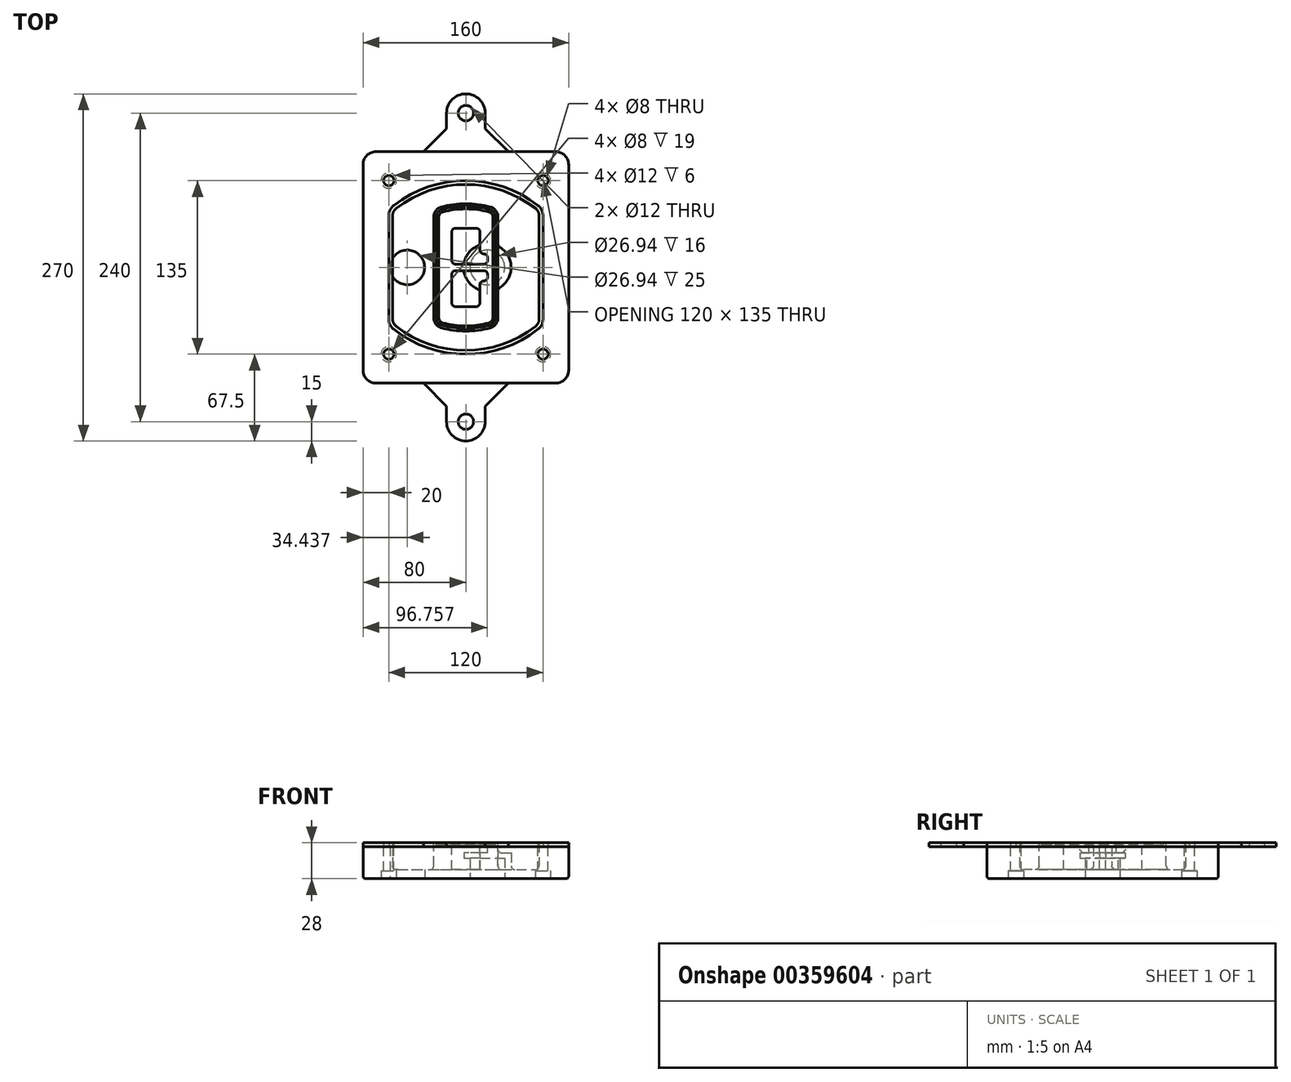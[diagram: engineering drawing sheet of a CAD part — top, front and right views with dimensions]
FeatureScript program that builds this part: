
annotation { "Feature Type Name" : "Feature", "Feature Type Description" : "" }
export const myFeature = defineFeature(function(context is Context, id is Id, definition is map)
    precondition{}
    {
        {
            var Q0;
            Q0=qCreatedBy(makeId("Top.planeOp"),FACE);
            var sketch = newSketch(context, id + "F0", { "sketchPlane" : qUnion([Q0])});
            skPoint(sketch, "E0.rect.middle", {"position": v(0, 0) * mm});
            skLineSegment(sketch, "E1.bottom", {"start": v(-70, -90) * mm, "end": v(70, -90) * mm});
            skLineSegment(sketch, "E1.top", {"start": v(-70, 90) * mm, "end": v(70, 90) * mm});
            skLineSegment(sketch, "E1.left", {"start": v(-80, -80) * mm, "end": v(-80, 80) * mm});
            skLineSegment(sketch, "E1.right", {"start": v(80, -80) * mm, "end": v(80, 80) * mm});
            skLineSegment(sketch, "E2", {"start": v(-80, 90) * mm, "end": v(80, -90) * mm, "construction": true});
            skLineSegment(sketch, "E3", {"start": v(80, 90) * mm, "end": v(-80, -90) * mm, "construction": true});
            skCircle(sketch, "E4", {"center": v(-60, 67.5) * mm, "radius": 4 * mm});
            skCircle(sketch, "E5", {"center": v(60, 67.5) * mm, "radius": 4 * mm});
            skCircle(sketch, "E6", {"center": v(60, -67.5) * mm, "radius": 4 * mm});
            skCircle(sketch, "E7", {"center": v(-60, -67.5) * mm, "radius": 4 * mm});
            skLineSegment(sketch, "E8", {"start": v(-60, 67.5) * mm, "end": v(60, 67.5) * mm, "construction": true});
            skLineSegment(sketch, "E9", {"start": v(60, 67.5) * mm, "end": v(60, -67.5) * mm, "construction": true});
            skLineSegment(sketch, "E10", {"start": v(60, -67.5) * mm, "end": v(-60, -67.5) * mm, "construction": true});
            skLineSegment(sketch, "E11", {"start": v(-60, -67.5) * mm, "end": v(-60, 67.5) * mm, "construction": true});
            skLineSegment(sketch, "E12", {"start": v(-60, 40.3) * mm, "end": v(-60, -40.3) * mm});
            skLineSegment(sketch, "E13", {"start": v(60, 40.3) * mm, "end": v(60, -40.3) * mm});
            skArc(sketch, "E14", {"start": v(56.15, 48.18) * mm, "mid": v(0, 67.5) * mm, "end": v(-56.15, 48.18) * mm});
            skArc(sketch, "E15", {"start": v(-56.15, -48.18) * mm, "mid": v(0, -67.5) * mm, "end": v(56.15, -48.18) * mm});
            skLineSegment(sketch, "E16", {"start": v(-60, 0) * mm, "end": v(60, 0) * mm, "construction": true});
            skPoint(sketch, "E17.visualSharp", {"position": v(-60, -45) * mm});
            skArc(sketch, "E17.filletArc", {"start": v(-60, -40.3) * mm, "mid": v(-58.99, -44.68) * mm, "end": v(-56.15, -48.18) * mm});
            skPoint(sketch, "E18.visualSharp", {"position": v(-60, 45) * mm});
            skArc(sketch, "E18.filletArc", {"start": v(-56.15, 48.18) * mm, "mid": v(-58.99, 44.68) * mm, "end": v(-60, 40.3) * mm});
            skPoint(sketch, "E19.visualSharp", {"position": v(60, 45) * mm});
            skArc(sketch, "E19.filletArc", {"start": v(60, 40.3) * mm, "mid": v(58.99, 44.68) * mm, "end": v(56.15, 48.18) * mm});
            skPoint(sketch, "E20.visualSharp", {"position": v(60, -45) * mm});
            skArc(sketch, "E20.filletArc", {"start": v(56.15, -48.18) * mm, "mid": v(58.99, -44.68) * mm, "end": v(60, -40.3) * mm});
            skPoint(sketch, "E21.visualSharp", {"position": v(-80, 90) * mm});
            skArc(sketch, "E21.filletArc", {"start": v(-70, 90) * mm, "mid": v(-77.07, 87.07) * mm, "end": v(-80, 80) * mm});
            skPoint(sketch, "E22.visualSharp", {"position": v(80, 90) * mm});
            skArc(sketch, "E22.filletArc", {"start": v(80, 80) * mm, "mid": v(77.07, 87.07) * mm, "end": v(70, 90) * mm});
            skPoint(sketch, "E23.visualSharp", {"position": v(80, -90) * mm});
            skArc(sketch, "E23.filletArc", {"start": v(70, -90) * mm, "mid": v(77.07, -87.07) * mm, "end": v(80, -80) * mm});
            skPoint(sketch, "E24.visualSharp", {"position": v(-80, -90) * mm});
            skArc(sketch, "E24.filletArc", {"start": v(-80, -80) * mm, "mid": v(-77.07, -87.07) * mm, "end": v(-70, -90) * mm});
            skArc(sketch, "E25.0", {"start": v(57, 40.3) * mm, "mid": v(56.3, 43.36) * mm, "end": v(54.3, 45.81) * mm});
            skLineSegment(sketch, "E25.1", {"start": v(57, 40.3) * mm, "end": v(57, -40.3) * mm});
            skArc(sketch, "E25.2", {"start": v(54.3, -45.81) * mm, "mid": v(56.3, -43.36) * mm, "end": v(57, -40.3) * mm});
            skArc(sketch, "E25.3", {"start": v(-54.3, -45.81) * mm, "mid": v(0, -64.5) * mm, "end": v(54.3, -45.81) * mm});
            skArc(sketch, "E25.4", {"start": v(-57, -40.3) * mm, "mid": v(-56.3, -43.36) * mm, "end": v(-54.3, -45.81) * mm});
            skArc(sketch, "E25.5", {"start": v(54.3, 45.81) * mm, "mid": v(0, 64.5) * mm, "end": v(-54.3, 45.81) * mm});
            skLineSegment(sketch, "E25.6", {"start": v(-57, 40.3) * mm, "end": v(-57, -40.3) * mm});
            skArc(sketch, "E25.7", {"start": v(-54.3, 45.81) * mm, "mid": v(-56.3, 43.36) * mm, "end": v(-57, 40.3) * mm});
            skArc(sketch, "E26.0", {"start": v(-58.62, 51.33) * mm, "mid": v(-62.58, 46.43) * mm, "end": v(-64, 40.3) * mm});
            skArc(sketch, "E26.1", {"start": v(58.62, 51.33) * mm, "mid": v(0, 71.5) * mm, "end": v(-58.62, 51.33) * mm});
            skArc(sketch, "E26.2", {"start": v(64, 40.3) * mm, "mid": v(62.58, 46.43) * mm, "end": v(58.62, 51.33) * mm});
            skLineSegment(sketch, "E26.3", {"start": v(64, 40.3) * mm, "end": v(64, -40.3) * mm});
            skArc(sketch, "E26.4", {"start": v(58.62, -51.33) * mm, "mid": v(62.58, -46.43) * mm, "end": v(64, -40.3) * mm});
            skLineSegment(sketch, "E26.5", {"start": v(-64, 40.3) * mm, "end": v(-64, -40.3) * mm});
            skArc(sketch, "E26.6", {"start": v(-58.62, -51.33) * mm, "mid": v(0, -71.5) * mm, "end": v(58.62, -51.33) * mm});
            skArc(sketch, "E26.7", {"start": v(-64, -40.3) * mm, "mid": v(-62.58, -46.43) * mm, "end": v(-58.62, -51.33) * mm});
            skSolve(sketch);
        }
        {
            var Q0;
            Q0=makeQuery(id+"F0.imprint","IMPRINT",FACE,{"disambiguationData":[TD([[makeQuery(id+"F0.imprint","IMPRINT",EDGE,{"derivedFrom":sQuery(id+"F0.wireOp",EDGE,"E1.bottom")}),1.0]])]});
            var Q1;
            Q1=makeQuery(id+"F0.imprint","IMPRINT",FACE,{"disambiguationData":[TD([[makeQuery(id+"F0.imprint","IMPRINT",EDGE,{"derivedFrom":sQuery(id+"F0.wireOp",EDGE,"E12")}),1.0]])]});
            var Q2;
            Q2=makeQuery(id+"F0.imprint","IMPRINT",FACE,{"disambiguationData":[TD([[makeQuery(id+"F0.imprint","IMPRINT",EDGE,{"derivedFrom":sQuery(id+"F0.wireOp",EDGE,"E25.0")}),1.0]])]});
            var Q3;
            Q3=makeQuery(id+"F0.imprint","IMPRINT",FACE,{"disambiguationData":[TD([[makeQuery(id+"F0.imprint","IMPRINT",EDGE,{"derivedFrom":sQuery(id+"F0.wireOp",EDGE,"E12")}),-1.0]])]});
            extrude(context, id + "F1", {"entities" : qUnion([Q0, Q1, Q2, Q3]), "oppositeDirection" : true, "depth" : 25 * mm});
        }
        {
            var Q0;
            Q0=makeQuery(id+"F0.imprint","IMPRINT",FACE,{"disambiguationData":[TD([[makeQuery(id+"F0.imprint","IMPRINT",EDGE,{"derivedFrom":sQuery(id+"F0.wireOp",EDGE,"E12")}),1.0]])]});
            extrude(context, id + "F2", {"entities" : qUnion([Q0]), "operationType" : NewBodyOperationType.ADD, "depth" : 3 * mm});
        }
        {
            var Q0;
            Q0=makeQuery(id+"F0.imprint","IMPRINT",FACE,{"disambiguationData":[TD([[makeQuery(id+"F0.imprint","IMPRINT",EDGE,{"derivedFrom":sQuery(id+"F0.wireOp",EDGE,"E25.0")}),1.0]])]});
            extrude(context, id + "F3", {"entities" : qUnion([Q0]), "operationType" : NewBodyOperationType.REMOVE, "oppositeDirection" : true, "depth" : 18 * mm});
        }
        {
            var Q0;
            Q0=makeQuery(id+"F2.opExtrude","CAP_FACE",FACE,{"disambiguationData":[OSD([sQuery(id+"F0.wireOp",EDGE,"E12"),sQuery(id+"F0.wireOp",EDGE,"E13"),sQuery(id+"F0.wireOp",EDGE,"E14"),sQuery(id+"F0.wireOp",EDGE,"E15"),sQuery(id+"F0.wireOp",EDGE,"E17.filletArc"),sQuery(id+"F0.wireOp",EDGE,"E18.filletArc"),sQuery(id+"F0.wireOp",EDGE,"E19.filletArc"),sQuery(id+"F0.wireOp",EDGE,"E20.filletArc"),sQuery(id+"F0.wireOp",EDGE,"E25.0"),sQuery(id+"F0.wireOp",EDGE,"E25.1"),sQuery(id+"F0.wireOp",EDGE,"E25.2"),sQuery(id+"F0.wireOp",EDGE,"E25.3"),sQuery(id+"F0.wireOp",EDGE,"E25.4"),sQuery(id+"F0.wireOp",EDGE,"E25.5"),sQuery(id+"F0.wireOp",EDGE,"E25.6"),sQuery(id+"F0.wireOp",EDGE,"E25.7")])],"isStart":false});
            var sketch = newSketch(context, id + "F4", { "sketchPlane" : qUnion([Q0])});
            skArc(sketch, "E27.0", {"start": v(-19.08, -46.97) * mm, "mid": v(0, -49.5) * mm, "end": v(19.08, -46.97) * mm});
            skArc(sketch, "E28.0", {"start": v(19.08, 46.97) * mm, "mid": v(0, 49.5) * mm, "end": v(-19.08, 46.97) * mm});
            skLineSegment(sketch, "E29", {"start": v(-25, 39.25) * mm, "end": v(-25, -39.25) * mm});
            skLineSegment(sketch, "E30", {"start": v(25, 39.25) * mm, "end": v(25, -39.25) * mm});
            skLineSegment(sketch, "E31", {"start": v(-25, 45.1) * mm, "end": v(25, 45.1) * mm, "construction": true});
            skLineSegment(sketch, "E32", {"start": v(-25, -45.1) * mm, "end": v(25, -45.1) * mm, "construction": true});
            skPoint(sketch, "E33.visualSharp", {"position": v(-25, 45.1) * mm});
            skArc(sketch, "E33.filletArc", {"start": v(-19.08, 46.97) * mm, "mid": v(-23.35, 44.11) * mm, "end": v(-25, 39.25) * mm});
            skPoint(sketch, "E34.visualSharp", {"position": v(25, 45.1) * mm});
            skArc(sketch, "E34.filletArc", {"start": v(25, 39.25) * mm, "mid": v(23.35, 44.11) * mm, "end": v(19.08, 46.97) * mm});
            skPoint(sketch, "E35.visualSharp", {"position": v(25, -45.1) * mm});
            skArc(sketch, "E35.filletArc", {"start": v(19.08, -46.97) * mm, "mid": v(23.35, -44.11) * mm, "end": v(25, -39.25) * mm});
            skPoint(sketch, "E36.visualSharp", {"position": v(-25, -45.1) * mm});
            skArc(sketch, "E36.filletArc", {"start": v(-25, -39.25) * mm, "mid": v(-23.35, -44.11) * mm, "end": v(-19.08, -46.97) * mm});
            skArc(sketch, "E37.0", {"start": v(54.3, 45.81) * mm, "mid": v(0, 64.5) * mm, "end": v(-54.3, 45.81) * mm});
            skArc(sketch, "E37.1", {"start": v(-54.3, 45.81) * mm, "mid": v(-56.3, 43.36) * mm, "end": v(-57, 40.3) * mm});
            skLineSegment(sketch, "E37.2", {"start": v(-57, 40.3) * mm, "end": v(-57, -40.3) * mm});
            skArc(sketch, "E37.3", {"start": v(-57, -40.3) * mm, "mid": v(-56.3, -43.36) * mm, "end": v(-54.3, -45.81) * mm});
            skArc(sketch, "E37.4", {"start": v(-54.3, -45.81) * mm, "mid": v(0, -64.5) * mm, "end": v(54.3, -45.81) * mm});
            skArc(sketch, "E37.5", {"start": v(54.3, -45.81) * mm, "mid": v(56.3, -43.36) * mm, "end": v(57, -40.3) * mm});
            skLineSegment(sketch, "E37.6", {"start": v(57, 40.3) * mm, "end": v(57, -40.3) * mm});
            skArc(sketch, "E37.7", {"start": v(57, 40.3) * mm, "mid": v(56.3, 43.36) * mm, "end": v(54.3, 45.81) * mm});
            skLineSegment(sketch, "E38.0", {"start": v(23, 39.25) * mm, "end": v(23, -39.25) * mm});
            skArc(sketch, "E38.1", {"start": v(18.56, -45.04) * mm, "mid": v(21.76, -42.9) * mm, "end": v(23, -39.25) * mm});
            skArc(sketch, "E38.2", {"start": v(-18.56, -45.04) * mm, "mid": v(0, -47.5) * mm, "end": v(18.56, -45.04) * mm});
            skArc(sketch, "E38.3", {"start": v(-23, -39.25) * mm, "mid": v(-21.76, -42.9) * mm, "end": v(-18.56, -45.04) * mm});
            skLineSegment(sketch, "E38.4", {"start": v(-23, 39.25) * mm, "end": v(-23, -39.25) * mm});
            skArc(sketch, "E38.5", {"start": v(23, 39.25) * mm, "mid": v(21.76, 42.9) * mm, "end": v(18.56, 45.04) * mm});
            skArc(sketch, "E38.6", {"start": v(-18.56, 45.04) * mm, "mid": v(-21.76, 42.9) * mm, "end": v(-23, 39.25) * mm});
            skArc(sketch, "E38.7", {"start": v(18.56, 45.04) * mm, "mid": v(0, 47.5) * mm, "end": v(-18.56, 45.04) * mm});
            skArc(sketch, "E39.0", {"start": v(21, 39.25) * mm, "mid": v(20.18, 41.68) * mm, "end": v(18.04, 43.1) * mm});
            skLineSegment(sketch, "E39.1", {"start": v(21, 39.25) * mm, "end": v(21, -39.25) * mm});
            skArc(sketch, "E39.2", {"start": v(18.04, -43.1) * mm, "mid": v(20.18, -41.68) * mm, "end": v(21, -39.25) * mm});
            skArc(sketch, "E39.3", {"start": v(-18.04, -43.1) * mm, "mid": v(0, -45.5) * mm, "end": v(18.04, -43.1) * mm});
            skArc(sketch, "E39.4", {"start": v(-21, -39.25) * mm, "mid": v(-20.18, -41.68) * mm, "end": v(-18.04, -43.1) * mm});
            skArc(sketch, "E39.5", {"start": v(18.04, 43.1) * mm, "mid": v(0, 45.5) * mm, "end": v(-18.04, 43.1) * mm});
            skLineSegment(sketch, "E39.6", {"start": v(-21, 39.25) * mm, "end": v(-21, -39.25) * mm});
            skArc(sketch, "E39.7", {"start": v(-18.04, 43.1) * mm, "mid": v(-20.18, 41.68) * mm, "end": v(-21, 39.25) * mm});
            skLineSegment(sketch, "E40", {"start": v(-25, 0) * mm, "end": v(25, 0) * mm, "construction": true});
            skLineSegment(sketch, "E41", {"start": v(-11, 5.5) * mm, "end": v(-11, 27.5) * mm});
            skLineSegment(sketch, "E42", {"start": v(-8, 30.5) * mm, "end": v(8, 30.5) * mm});
            skLineSegment(sketch, "E43", {"start": v(11, 27.5) * mm, "end": v(11, 13.5) * mm});
            skLineSegment(sketch, "E44", {"start": v(14, 10.5) * mm, "end": v(14, 10.5) * mm});
            skLineSegment(sketch, "E45", {"start": v(17, 7.5) * mm, "end": v(17, 5.5) * mm});
            skLineSegment(sketch, "E46", {"start": v(14, 2.5) * mm, "end": v(-8, 2.5) * mm});
            skPoint(sketch, "E47.visualSharp", {"position": v(-11, 30.5) * mm});
            skArc(sketch, "E47.filletArc", {"start": v(-8, 30.5) * mm, "mid": v(-10.12, 29.62) * mm, "end": v(-11, 27.5) * mm});
            skPoint(sketch, "E48.visualSharp", {"position": v(11, 30.5) * mm});
            skArc(sketch, "E48.filletArc", {"start": v(11, 27.5) * mm, "mid": v(10.12, 29.62) * mm, "end": v(8, 30.5) * mm});
            skPoint(sketch, "E49.visualSharp", {"position": v(11, 10.5) * mm});
            skArc(sketch, "E49.filletArc", {"start": v(11, 13.5) * mm, "mid": v(11.88, 11.38) * mm, "end": v(14, 10.5) * mm});
            skPoint(sketch, "E50.visualSharp", {"position": v(17, 10.5) * mm});
            skArc(sketch, "E50.filletArc", {"start": v(17, 7.5) * mm, "mid": v(16.12, 9.62) * mm, "end": v(14, 10.5) * mm});
            skPoint(sketch, "E51.visualSharp", {"position": v(17, 2.5) * mm});
            skArc(sketch, "E51.filletArc", {"start": v(14, 2.5) * mm, "mid": v(16.12, 3.38) * mm, "end": v(17, 5.5) * mm});
            skPoint(sketch, "E52.visualSharp", {"position": v(-11, 2.5) * mm});
            skArc(sketch, "E52.filletArc", {"start": v(-11, 5.5) * mm, "mid": v(-10.12, 3.38) * mm, "end": v(-8, 2.5) * mm});
            skLineSegment(sketch, "E53.0.MirrorCS", {"start": v(14, -2.5) * mm, "end": v(-8, -2.5) * mm});
            skArc(sketch, "E54.0.MirrorCS", {"start": v(-11, -5.5) * mm, "mid": v(-10.12, -3.38) * mm, "end": v(-8, -2.5) * mm});
            skLineSegment(sketch, "E55.0.MirrorCS", {"start": v(-11, -5.5) * mm, "end": v(-11, -27.5) * mm});
            skArc(sketch, "E56.0.MirrorCS", {"start": v(-8, -30.5) * mm, "mid": v(-10.12, -29.62) * mm, "end": v(-11, -27.5) * mm});
            skLineSegment(sketch, "E57.0.MirrorCS", {"start": v(-8, -30.5) * mm, "end": v(8, -30.5) * mm});
            skArc(sketch, "E58.0.MirrorCS", {"start": v(11, -27.5) * mm, "mid": v(10.12, -29.62) * mm, "end": v(8, -30.5) * mm});
            skLineSegment(sketch, "E59.0.MirrorCS", {"start": v(11, -27.5) * mm, "end": v(11, -13.5) * mm});
            skArc(sketch, "E60.0.MirrorCS", {"start": v(11, -13.5) * mm, "mid": v(11.88, -11.38) * mm, "end": v(14, -10.5) * mm});
            skArc(sketch, "E61.0.MirrorCS", {"start": v(17, -7.5) * mm, "mid": v(16.12, -9.62) * mm, "end": v(14, -10.5) * mm});
            skLineSegment(sketch, "E62.0.MirrorCS", {"start": v(17, -7.5) * mm, "end": v(17, -5.5) * mm});
            skArc(sketch, "E63.0.MirrorCS", {"start": v(14, -2.5) * mm, "mid": v(16.12, -3.38) * mm, "end": v(17, -5.5) * mm});
            skSolve(sketch);
        }
        {
            var Q0;
            Q0=makeQuery(id+"F4.imprint","IMPRINT",FACE,{"disambiguationData":[TD([[makeQuery(id+"F4.imprint","IMPRINT",EDGE,{"derivedFrom":sQuery(id+"F4.wireOp",EDGE,"E27.0")}),1.0]])]});
            var Q1;
            Q1=makeQuery(id+"F4.imprint","IMPRINT",FACE,{"disambiguationData":[TD([[makeQuery(id+"F4.imprint","IMPRINT",EDGE,{"derivedFrom":sQuery(id+"F4.wireOp",EDGE,"E38.0")}),-1.0]])]});
            var Q2;
            Q2=makeQuery(id+"F4.imprint","IMPRINT",FACE,{"disambiguationData":[TD([[makeQuery(id+"F4.imprint","IMPRINT",EDGE,{"derivedFrom":sQuery(id+"F4.wireOp",EDGE,"E39.0")}),1.0]])]});
            extrude(context, id + "F5", {"entities" : qUnion([Q0, Q1, Q2]), "operationType" : NewBodyOperationType.ADD, "endBound" : BoundingType.UP_TO_NEXT, "oppositeDirection" : true, "depth" : 25 * mm});
        }
        {
            var Q0;
            Q0=makeQuery(id+"F4.imprint","IMPRINT",FACE,{"disambiguationData":[TD([[makeQuery(id+"F4.imprint","IMPRINT",EDGE,{"derivedFrom":sQuery(id+"F4.wireOp",EDGE,"E38.0")}),-1.0]])]});
            extrude(context, id + "F6", {"entities" : qUnion([Q0]), "operationType" : NewBodyOperationType.REMOVE, "oppositeDirection" : true, "depth" : 2 * mm});
        }
        {
            var Q0;
            Q0=makeQuery(id+"F1.opExtrude","CAP_FACE",FACE,{"disambiguationData":[OSD([sQuery(id+"F0.wireOp",EDGE,"E1.bottom"),sQuery(id+"F0.wireOp",EDGE,"E1.top"),sQuery(id+"F0.wireOp",EDGE,"E1.left"),sQuery(id+"F0.wireOp",EDGE,"E1.right"),sQuery(id+"F0.wireOp",EDGE,"E4"),sQuery(id+"F0.wireOp",EDGE,"E5"),sQuery(id+"F0.wireOp",EDGE,"E6"),sQuery(id+"F0.wireOp",EDGE,"E7"),sQuery(id+"F0.wireOp",EDGE,"E21.filletArc"),sQuery(id+"F0.wireOp",EDGE,"E22.filletArc"),sQuery(id+"F0.wireOp",EDGE,"E23.filletArc"),sQuery(id+"F0.wireOp",EDGE,"E24.filletArc")])],"isStart":false});
            var sketch = newSketch(context, id + "F7", { "sketchPlane" : qUnion([Q0])});
            skCircle(sketch, "E64", {"center": v(16.76, 0) * mm, "radius": 13.47 * mm});
            skCircle(sketch, "E65", {"center": v(-45.56, 0) * mm, "radius": 13.47 * mm});
            skLineSegment(sketch, "E66", {"start": v(80, 0) * mm, "end": v(-80, 0) * mm});
            skCircle(sketch, "E67", {"center": v(16.76, 0) * mm, "radius": 18.47 * mm});
            skCircle(sketch, "E68", {"center": v(60, -67.5) * mm, "radius": 6 * mm});
            skCircle(sketch, "E69", {"center": v(-60, -67.5) * mm, "radius": 6 * mm});
            skCircle(sketch, "E70", {"center": v(-60, 67.5) * mm, "radius": 6 * mm});
            skCircle(sketch, "E71", {"center": v(60, 67.5) * mm, "radius": 6 * mm});
            skSolve(sketch);
        }
        {
            var Q0;
            {var subQ1=sQuery(id+"F7.wireOp",EDGE,"E66");var subQ4=sQuery(id+"F7.wireOp",EDGE,"E64");var subQ6=makeQuery(id+"F7.imprint","INTERSECT",VERTEX,{"disambiguationData":[OD(0.0)],"derivedFrom":[subQ4,subQ1]});Q0=makeQuery(id+"F7.imprint","IMPRINT",FACE,{"disambiguationData":[TD([[makeQuery(id+"F7.imprint","IMPRINT",EDGE,{"disambiguationData":[TD([[subQ6,-1.0]])],"derivedFrom":subQ4}),-1.0]])]});}
            var Q1;
            {var subQ0=sQuery(id+"F7.wireOp",EDGE,"E66");var subQ1=sQuery(id+"F7.wireOp",EDGE,"E64");var subQ3=makeQuery(id+"F7.imprint","INTERSECT",VERTEX,{"disambiguationData":[OD(0.0)],"derivedFrom":[subQ1,subQ0]});Q1=makeQuery(id+"F7.imprint","IMPRINT",FACE,{"disambiguationData":[TD([[makeQuery(id+"F7.imprint","IMPRINT",EDGE,{"disambiguationData":[TD([[subQ3,-1.0]])],"derivedFrom":subQ1}),1.0]])]});}
            var Q2;
            {var subQ0=sQuery(id+"F7.wireOp",EDGE,"E66");var subQ1=sQuery(id+"F7.wireOp",EDGE,"E64");var subQ3=makeQuery(id+"F7.imprint","INTERSECT",VERTEX,{"disambiguationData":[OD(0.0)],"derivedFrom":[subQ1,subQ0]});Q2=makeQuery(id+"F7.imprint","IMPRINT",FACE,{"disambiguationData":[TD([[makeQuery(id+"F7.imprint","IMPRINT",EDGE,{"disambiguationData":[TD([[subQ3,1.0]])],"derivedFrom":subQ1}),1.0]])]});}
            var Q3;
            {var subQ1=sQuery(id+"F7.wireOp",EDGE,"E66");var subQ4=sQuery(id+"F7.wireOp",EDGE,"E64");var subQ6=makeQuery(id+"F7.imprint","INTERSECT",VERTEX,{"disambiguationData":[OD(0.0)],"derivedFrom":[subQ4,subQ1]});Q3=makeQuery(id+"F7.imprint","IMPRINT",FACE,{"disambiguationData":[TD([[makeQuery(id+"F7.imprint","IMPRINT",EDGE,{"disambiguationData":[TD([[subQ6,1.0]])],"derivedFrom":subQ4}),-1.0]])]});}
            extrude(context, id + "F8", {"entities" : qUnion([Q0, Q1, Q2, Q3]), "operationType" : NewBodyOperationType.ADD, "oppositeDirection" : true, "depth" : 20 * mm});
        }
        {
            var Q0;
            {var subQ0=sQuery(id+"F7.wireOp",EDGE,"E66");var subQ1=sQuery(id+"F7.wireOp",EDGE,"E64");var subQ3=makeQuery(id+"F7.imprint","INTERSECT",VERTEX,{"disambiguationData":[OD(0.0)],"derivedFrom":[subQ1,subQ0]});Q0=makeQuery(id+"F7.imprint","IMPRINT",FACE,{"disambiguationData":[TD([[makeQuery(id+"F7.imprint","IMPRINT",EDGE,{"disambiguationData":[TD([[subQ3,-1.0]])],"derivedFrom":subQ1}),1.0]])]});}
            var Q1;
            {var subQ0=sQuery(id+"F7.wireOp",EDGE,"E66");var subQ1=sQuery(id+"F7.wireOp",EDGE,"E64");var subQ3=makeQuery(id+"F7.imprint","INTERSECT",VERTEX,{"disambiguationData":[OD(0.0)],"derivedFrom":[subQ1,subQ0]});Q1=makeQuery(id+"F7.imprint","IMPRINT",FACE,{"disambiguationData":[TD([[makeQuery(id+"F7.imprint","IMPRINT",EDGE,{"disambiguationData":[TD([[subQ3,1.0]])],"derivedFrom":subQ1}),1.0]])]});}
            extrude(context, id + "F9", {"entities" : qUnion([Q0, Q1]), "operationType" : NewBodyOperationType.REMOVE, "oppositeDirection" : true, "depth" : 16 * mm});
        }
        {
            var Q0;
            {var subQ0=sQuery(id+"F7.wireOp",EDGE,"E66");var subQ1=sQuery(id+"F7.wireOp",EDGE,"E65");var subQ3=makeQuery(id+"F7.imprint","INTERSECT",VERTEX,{"disambiguationData":[OD(0.0)],"derivedFrom":[subQ1,subQ0]});Q0=makeQuery(id+"F7.imprint","IMPRINT",FACE,{"disambiguationData":[TD([[makeQuery(id+"F7.imprint","IMPRINT",EDGE,{"disambiguationData":[TD([[subQ3,-1.0]])],"derivedFrom":subQ1}),1.0]])]});}
            var Q1;
            {var subQ0=sQuery(id+"F7.wireOp",EDGE,"E66");var subQ1=sQuery(id+"F7.wireOp",EDGE,"E65");var subQ3=makeQuery(id+"F7.imprint","INTERSECT",VERTEX,{"disambiguationData":[OD(0.0)],"derivedFrom":[subQ1,subQ0]});Q1=makeQuery(id+"F7.imprint","IMPRINT",FACE,{"disambiguationData":[TD([[makeQuery(id+"F7.imprint","IMPRINT",EDGE,{"disambiguationData":[TD([[subQ3,1.0]])],"derivedFrom":subQ1}),1.0]])]});}
            extrude(context, id + "F10", {"entities" : qUnion([Q0, Q1]), "operationType" : NewBodyOperationType.REMOVE, "oppositeDirection" : true, "depth" : 25 * mm});
        }
        {
            var Q0;
            Q0=makeQuery(id+"F7.imprint","IMPRINT",FACE,{"disambiguationData":[TD([[makeQuery(id+"F7.imprint","IMPRINT",EDGE,{"derivedFrom":sQuery(id+"F7.wireOp",EDGE,"E68")}),1.0]])]});
            var Q1;
            Q1=makeQuery(id+"F7.imprint","IMPRINT",FACE,{"disambiguationData":[TD([[makeQuery(id+"F7.imprint","IMPRINT",EDGE,{"derivedFrom":makeQuery(id+"F1.opExtrude","CAP_EDGE",EDGE,{"disambiguationData":[OSD([sQuery(id+"F0.wireOp",EDGE,"E5")])],"isStart":false})}),-1.0]])]});
            var Q2;
            Q2=makeQuery(id+"F7.imprint","IMPRINT",FACE,{"disambiguationData":[TD([[makeQuery(id+"F7.imprint","IMPRINT",EDGE,{"derivedFrom":sQuery(id+"F7.wireOp",EDGE,"E69")}),1.0]])]});
            var Q3;
            Q3=makeQuery(id+"F7.imprint","IMPRINT",FACE,{"disambiguationData":[TD([[makeQuery(id+"F7.imprint","IMPRINT",EDGE,{"derivedFrom":makeQuery(id+"F1.opExtrude","CAP_EDGE",EDGE,{"disambiguationData":[OSD([sQuery(id+"F0.wireOp",EDGE,"E4")])],"isStart":false})}),-1.0]])]});
            var Q4;
            Q4=makeQuery(id+"F7.imprint","IMPRINT",FACE,{"disambiguationData":[TD([[makeQuery(id+"F7.imprint","IMPRINT",EDGE,{"derivedFrom":sQuery(id+"F7.wireOp",EDGE,"E70")}),1.0]])]});
            var Q5;
            Q5=makeQuery(id+"F7.imprint","IMPRINT",FACE,{"disambiguationData":[TD([[makeQuery(id+"F7.imprint","IMPRINT",EDGE,{"derivedFrom":makeQuery(id+"F1.opExtrude","CAP_EDGE",EDGE,{"disambiguationData":[OSD([sQuery(id+"F0.wireOp",EDGE,"E7")])],"isStart":false})}),-1.0]])]});
            var Q6;
            Q6=makeQuery(id+"F7.imprint","IMPRINT",FACE,{"disambiguationData":[TD([[makeQuery(id+"F7.imprint","IMPRINT",EDGE,{"derivedFrom":sQuery(id+"F7.wireOp",EDGE,"E71")}),1.0]])]});
            var Q7;
            Q7=makeQuery(id+"F7.imprint","IMPRINT",FACE,{"disambiguationData":[TD([[makeQuery(id+"F7.imprint","IMPRINT",EDGE,{"derivedFrom":makeQuery(id+"F1.opExtrude","CAP_EDGE",EDGE,{"disambiguationData":[OSD([sQuery(id+"F0.wireOp",EDGE,"E6")])],"isStart":false})}),-1.0]])]});
            extrude(context, id + "F11", {"entities" : qUnion([Q0, Q1, Q2, Q3, Q4, Q5, Q6, Q7]), "operationType" : NewBodyOperationType.REMOVE, "oppositeDirection" : true, "depth" : 6 * mm});
        }
        {
            var Q0;
            Q0=makeQuery(id+"F9.boolean.opBoolean","COPY",FACE,{"derivedFrom":makeQuery(id+"F9.opExtrude","CAP_FACE",FACE,{"disambiguationData":[OSD([sQuery(id+"F7.wireOp",EDGE,"E64")])],"isStart":false})});
            var sketch = newSketch(context, id + "F12", { "sketchPlane" : qUnion([Q0])});
            skArc(sketch, "E72.0", {"start": v(11, 17.55) * mm, "mid": v(2.57, 11.82) * mm, "end": v(-1.54, 2.5) * mm});
            skArc(sketch, "E72.1", {"start": v(-1.54, -2.5) * mm, "mid": v(2.57, -11.82) * mm, "end": v(11, -17.55) * mm});
            skLineSegment(sketch, "E73", {"start": v(-1.54, -2.5) * mm, "end": v(14, -2.5) * mm});
            skLineSegment(sketch, "E74.0", {"start": v(14, 2.5) * mm, "end": v(-1.54, 2.5) * mm});
            skArc(sketch, "E74.1", {"start": v(14, 2.5) * mm, "mid": v(16.12, 3.38) * mm, "end": v(17, 5.5) * mm});
            skLineSegment(sketch, "E74.2", {"start": v(17, 7.5) * mm, "end": v(17, 5.5) * mm});
            skArc(sketch, "E74.3", {"start": v(17, 7.5) * mm, "mid": v(16.12, 9.62) * mm, "end": v(14, 10.5) * mm});
            skArc(sketch, "E74.4", {"start": v(11, 13.5) * mm, "mid": v(11.88, 11.38) * mm, "end": v(14, 10.5) * mm});
            skLineSegment(sketch, "E74.5", {"start": v(11, 17.55) * mm, "end": v(11, 13.5) * mm});
            skLineSegment(sketch, "E74.7", {"start": v(14, -2.5) * mm, "end": v(-1.54, -2.5) * mm});
            skArc(sketch, "E74.8", {"start": v(14, -2.5) * mm, "mid": v(16.12, -3.38) * mm, "end": v(17, -5.5) * mm});
            skLineSegment(sketch, "E74.9", {"start": v(17, -7.5) * mm, "end": v(17, -5.5) * mm});
            skArc(sketch, "E74.10", {"start": v(17, -7.5) * mm, "mid": v(16.12, -9.62) * mm, "end": v(14, -10.5) * mm});
            skArc(sketch, "E74.11", {"start": v(11, -13.5) * mm, "mid": v(11.88, -11.38) * mm, "end": v(14, -10.5) * mm});
            skLineSegment(sketch, "E74.12", {"start": v(11, -17.55) * mm, "end": v(11, -13.5) * mm});
            skPoint(sketch, "E75.orphan", {"position": v(11, -27.5) * mm});
            skPoint(sketch, "E76.orphan", {"position": v(-8, -2.5) * mm});
            skPoint(sketch, "E77.orphan", {"position": v(-8, 2.5) * mm});
            skPoint(sketch, "E78.orphan", {"position": v(11, 27.5) * mm});
            skSolve(sketch);
        }
        {
            var Q0;
            {var subQ7=sQuery(id+"F12.wireOp",EDGE,"E72.0");var subQ14=sQuery(id+"F12.wireOp",EDGE,"E72.1");var subQ16=sQuery(id+"F12.wireOp",EDGE,"E74.1");var subQ18=sQuery(id+"F12.wireOp",EDGE,"E74.8");Q0=qUnion([makeQuery(id+"F12.imprint","IMPRINT",FACE,{"disambiguationData":[TD([[makeQuery(id+"F12.imprint","IMPRINT",EDGE,{"derivedFrom":subQ7}),1.0]])]}),makeQuery(id+"F12.imprint","IMPRINT",FACE,{"disambiguationData":[TD([[makeQuery(id+"F12.imprint","IMPRINT",EDGE,{"derivedFrom":subQ14}),1.0]])]}),makeQuery(id+"F12.imprint","IMPRINT",FACE,{"disambiguationData":[TD([[makeQuery(id+"F12.imprint","IMPRINT",EDGE,{"derivedFrom":subQ16}),1.0]])]}),makeQuery(id+"F12.imprint","IMPRINT",FACE,{"disambiguationData":[TD([[makeQuery(id+"F12.imprint","IMPRINT",EDGE,{"derivedFrom":subQ18}),-1.0]])]})]);}
            var Q1;
            Q1=makeQuery(id+"F5.boolean.opBoolean","SPLIT",FACE,{"disambiguationData":[TD([makeQuery(id+"F5.opExtrude","SWEPT_FACE",FACE,{"disambiguationData":[OSD([sQuery(id+"F4.wireOp",EDGE,"E41")])]})])],"derivedFrom":makeQuery(id+"F3.boolean.opBoolean","COPY",FACE,{"derivedFrom":makeQuery(id+"F3.opExtrude","CAP_FACE",FACE,{"disambiguationData":[OSD([sQuery(id+"F0.wireOp",EDGE,"E25.0"),sQuery(id+"F0.wireOp",EDGE,"E25.1"),sQuery(id+"F0.wireOp",EDGE,"E25.2"),sQuery(id+"F0.wireOp",EDGE,"E25.3"),sQuery(id+"F0.wireOp",EDGE,"E25.4"),sQuery(id+"F0.wireOp",EDGE,"E25.5"),sQuery(id+"F0.wireOp",EDGE,"E25.6"),sQuery(id+"F0.wireOp",EDGE,"E25.7")])],"isStart":false})})});
            extrude(context, id + "F13", {"entities" : qUnion([Q0]), "operationType" : NewBodyOperationType.REMOVE, "endBound" : BoundingType.UP_TO_SURFACE, "endBoundEntityFace" : qUnion([Q1]), "depth" : 25 * mm});
        }
        {
            var Q0;
            Q0=makeQuery(id+"F3.boolean.opBoolean","COPY",EDGE,{"derivedFrom":makeQuery(id+"F3.opExtrude","CAP_EDGE",EDGE,{"disambiguationData":[OSD([sQuery(id+"F0.wireOp",EDGE,"E25.6")])],"isStart":false})});
            var Q1;
            Q1=makeQuery(id+"F8.boolean.opBoolean","INTERSECT",EDGE,{"derivedFrom":[makeQuery(id+"F5.opExtrude","SWEPT_FACE",FACE,{"disambiguationData":[OSD([sQuery(id+"F4.wireOp",EDGE,"E30")])]}),makeQuery(id+"F8.opExtrude","CAP_FACE",FACE,{"disambiguationData":[OSD([sQuery(id+"F7.wireOp",EDGE,"E67")])],"isStart":false})]});
            var Q2;
            Q2=makeQuery(id+"F8.boolean.opBoolean","INTERSECT",EDGE,{"disambiguationData":[OD(1.0)],"derivedFrom":[makeQuery(id+"F5.opExtrude","SWEPT_FACE",FACE,{"disambiguationData":[OSD([sQuery(id+"F4.wireOp",EDGE,"E30")])]}),makeQuery(id+"F8.opExtrude","SWEPT_FACE",FACE,{"disambiguationData":[OSD([sQuery(id+"F7.wireOp",EDGE,"E67")])]})]});
            var Q3;
            {var subQ0=sQuery(id+"F4.wireOp",EDGE,"E30");Q3=makeQuery(id+"F8.boolean.opBoolean","SPLIT",EDGE,{"disambiguationData":[TD([makeQuery(id+"F5.opExtrude","SWEPT_FACE",FACE,{"disambiguationData":[OSD([sQuery(id+"F4.wireOp",EDGE,"E35.filletArc")])]})])],"derivedFrom":makeQuery(id+"F5.opExtrude","CAP_EDGE",EDGE,{"disambiguationData":[OSD([subQ0])],"isStart":false})});}
            var Q4;
            {var subQ0=sQuery(id+"F0.wireOp",EDGE,"E25.7");var subQ1=sQuery(id+"F0.wireOp",EDGE,"E25.1");var subQ2=sQuery(id+"F0.wireOp",EDGE,"E25.6");var subQ3=sQuery(id+"F0.wireOp",EDGE,"E25.5");var subQ4=sQuery(id+"F0.wireOp",EDGE,"E25.4");var subQ5=sQuery(id+"F0.wireOp",EDGE,"E25.0");var subQ6=sQuery(id+"F0.wireOp",EDGE,"E25.2");var subQ7=sQuery(id+"F0.wireOp",EDGE,"E25.3");Q4=makeQuery(id+"F8.boolean.opBoolean","INTERSECT",EDGE,{"derivedFrom":[makeQuery(id+"F5.boolean.opBoolean","SPLIT",FACE,{"disambiguationData":[TD([makeQuery(id+"F2.opExtrude","SWEPT_FACE",FACE,{"disambiguationData":[OSD([subQ5])]})])],"derivedFrom":makeQuery(id+"F3.boolean.opBoolean","COPY",FACE,{"derivedFrom":makeQuery(id+"F3.opExtrude","CAP_FACE",FACE,{"disambiguationData":[OSD([subQ5,subQ1,subQ6,subQ7,subQ4,subQ3,subQ2,subQ0])],"isStart":false})})}),makeQuery(id+"F8.opExtrude","SWEPT_FACE",FACE,{"disambiguationData":[OSD([sQuery(id+"F7.wireOp",EDGE,"E67")])]})]});}
            var Q5;
            Q5=makeQuery(id+"F8.boolean.opBoolean","INTERSECT",EDGE,{"disambiguationData":[OD(0.0)],"derivedFrom":[makeQuery(id+"F5.opExtrude","SWEPT_FACE",FACE,{"disambiguationData":[OSD([sQuery(id+"F4.wireOp",EDGE,"E30")])]}),makeQuery(id+"F8.opExtrude","SWEPT_FACE",FACE,{"disambiguationData":[OSD([sQuery(id+"F7.wireOp",EDGE,"E67")])]})]});
            fillet(context, id + "F14", {"entities" : qUnion([Q0, Q1, Q2, Q3, Q4, Q5]), "radius" : 3 * mm, "tangentPropagation" : true, "allowEdgeOverflow" : false});
        }
        {
            var Q0;
            Q0=makeQuery(id+"F1.opExtrude","CAP_EDGE",EDGE,{"disambiguationData":[OSD([sQuery(id+"F0.wireOp",EDGE,"E1.bottom")])],"isStart":false});
            fillet(context, id + "F15", {"entities" : qUnion([Q0]), "radius" : 2 * mm, "tangentPropagation" : true, "allowEdgeOverflow" : false});
        }
        {
            var Q0;
            {var subQ0=sQuery(id+"F0.wireOp",EDGE,"E21.filletArc");var subQ1=sQuery(id+"F0.wireOp",EDGE,"E7");var subQ2=sQuery(id+"F0.wireOp",EDGE,"E6");var subQ3=sQuery(id+"F0.wireOp",EDGE,"E5");var subQ4=sQuery(id+"F0.wireOp",EDGE,"E4");var subQ5=sQuery(id+"F0.wireOp",EDGE,"E22.filletArc");var subQ6=sQuery(id+"F0.wireOp",EDGE,"E1.bottom");var subQ7=sQuery(id+"F0.wireOp",EDGE,"E1.right");var subQ8=sQuery(id+"F0.wireOp",EDGE,"E1.top");var subQ9=sQuery(id+"F0.wireOp",EDGE,"E1.left");var subQ10=sQuery(id+"F0.wireOp",EDGE,"E23.filletArc");var subQ11=sQuery(id+"F0.wireOp",EDGE,"E24.filletArc");Q0=makeQuery(id+"F2.boolean.opBoolean","SPLIT",FACE,{"disambiguationData":[TD([makeQuery(id+"F1.opExtrude","SWEPT_FACE",FACE,{"disambiguationData":[OSD([subQ6])]})])],"derivedFrom":makeQuery(id+"F1.opExtrude","CAP_FACE",FACE,{"disambiguationData":[OSD([subQ6,subQ8,subQ9,subQ7,subQ4,subQ3,subQ2,subQ1,subQ0,subQ5,subQ10,subQ11])],"isStart":true})});}
            var sketch = newSketch(context, id + "F16", { "sketchPlane" : qUnion([Q0])});
            skLineSegment(sketch, "E79", {"start": v(33, 90) * mm, "end": v(15, 108) * mm});
            skCircle(sketch, "E80", {"center": v(0, 120) * mm, "radius": 6 * mm});
            skPoint(sketch, "E80.centerSnap0", {"position": v(0, 90) * mm});
            skArc(sketch, "E81", {"start": v(15, 120) * mm, "mid": v(0, 135) * mm, "end": v(-15, 120) * mm});
            skLineSegment(sketch, "E82", {"start": v(15, 120) * mm, "end": v(15, 108) * mm});
            skLineSegment(sketch, "E83", {"start": v(-15, 120) * mm, "end": v(-15, 108) * mm});
            skLineSegment(sketch, "E84", {"start": v(-15, 108) * mm, "end": v(-33, 90) * mm});
            skLineSegment(sketch, "E85", {"start": v(0, 114) * mm, "end": v(0, 90) * mm, "construction": true});
            skLineSegment(sketch, "E86", {"start": v(-33, 90) * mm, "end": v(33, 90) * mm});
            skLineSegment(sketch, "E87", {"start": v(-80, 0) * mm, "end": v(80, 0) * mm, "construction": true});
            skLineSegment(sketch, "E88.MirrorCS", {"start": v(-15, -120) * mm, "end": v(-15, -108) * mm});
            skLineSegment(sketch, "E89.MirrorCS", {"start": v(15, -120) * mm, "end": v(15, -108) * mm});
            skLineSegment(sketch, "E90.MirrorCS", {"start": v(33, -90) * mm, "end": v(15, -108) * mm});
            skLineSegment(sketch, "E91.MirrorCS", {"start": v(-15, -108) * mm, "end": v(-33, -90) * mm});
            skLineSegment(sketch, "E92.MirrorCS", {"start": v(-33, -90) * mm, "end": v(33, -90) * mm});
            skPoint(sketch, "E93.MirrorP", {"position": v(0, -90) * mm});
            skLineSegment(sketch, "E94.MirrorCS", {"start": v(0, -114) * mm, "end": v(0, -90) * mm, "construction": true});
            skArc(sketch, "E95.MirrorCS", {"start": v(15, -120) * mm, "mid": v(0, -135) * mm, "end": v(-15, -120) * mm});
            skCircle(sketch, "E96.MirrorC", {"center": v(0, -120) * mm, "radius": 6 * mm});
            skSolve(sketch);
        }
        {
            var Q0;
            Q0 = qSketchRegion(id + "F16", true);
            var Q1;
            Q1=makeQuery(id+"F2.opExtrude","CAP_FACE",FACE,{"disambiguationData":[OSD([sQuery(id+"F0.wireOp",EDGE,"E12"),sQuery(id+"F0.wireOp",EDGE,"E13"),sQuery(id+"F0.wireOp",EDGE,"E14"),sQuery(id+"F0.wireOp",EDGE,"E15"),sQuery(id+"F0.wireOp",EDGE,"E17.filletArc"),sQuery(id+"F0.wireOp",EDGE,"E18.filletArc"),sQuery(id+"F0.wireOp",EDGE,"E19.filletArc"),sQuery(id+"F0.wireOp",EDGE,"E20.filletArc"),sQuery(id+"F0.wireOp",EDGE,"E25.0"),sQuery(id+"F0.wireOp",EDGE,"E25.1"),sQuery(id+"F0.wireOp",EDGE,"E25.2"),sQuery(id+"F0.wireOp",EDGE,"E25.3"),sQuery(id+"F0.wireOp",EDGE,"E25.4"),sQuery(id+"F0.wireOp",EDGE,"E25.5"),sQuery(id+"F0.wireOp",EDGE,"E25.6"),sQuery(id+"F0.wireOp",EDGE,"E25.7")])],"isStart":false});
            extrude(context, id + "F17", {"entities" : qUnion([Q0]), "endBound" : BoundingType.UP_TO_SURFACE, "endBoundEntityFace" : qUnion([Q1]), "depth" : 25 * mm});
        }
        {
            var Q0;
            {var subQ0=sQuery(id+"F0.wireOp",EDGE,"E21.filletArc");var subQ1=sQuery(id+"F0.wireOp",EDGE,"E7");var subQ2=sQuery(id+"F0.wireOp",EDGE,"E6");var subQ3=sQuery(id+"F0.wireOp",EDGE,"E5");var subQ4=sQuery(id+"F0.wireOp",EDGE,"E4");var subQ5=sQuery(id+"F0.wireOp",EDGE,"E22.filletArc");var subQ6=sQuery(id+"F0.wireOp",EDGE,"E1.bottom");var subQ7=sQuery(id+"F0.wireOp",EDGE,"E1.right");var subQ8=sQuery(id+"F0.wireOp",EDGE,"E1.top");var subQ9=sQuery(id+"F0.wireOp",EDGE,"E1.left");var subQ10=sQuery(id+"F0.wireOp",EDGE,"E23.filletArc");var subQ11=sQuery(id+"F0.wireOp",EDGE,"E24.filletArc");Q0=makeQuery(id+"F2.boolean.opBoolean","SPLIT",FACE,{"disambiguationData":[TD([makeQuery(id+"F1.opExtrude","SWEPT_FACE",FACE,{"disambiguationData":[OSD([subQ6])]})])],"derivedFrom":makeQuery(id+"F1.opExtrude","CAP_FACE",FACE,{"disambiguationData":[OSD([subQ6,subQ8,subQ9,subQ7,subQ4,subQ3,subQ2,subQ1,subQ0,subQ5,subQ10,subQ11])],"isStart":true})});}
            var Q1;
            {Q1=qUnion([makeQuery(id+"F17.opExtrude","CAP_FACE",FACE,{"disambiguationData":[OSD([sQuery(id+"F16.wireOp",EDGE,"E79"),sQuery(id+"F16.wireOp",EDGE,"E80"),sQuery(id+"F16.wireOp",EDGE,"E81"),sQuery(id+"F16.wireOp",EDGE,"E82"),sQuery(id+"F16.wireOp",EDGE,"E83"),sQuery(id+"F16.wireOp",EDGE,"E84"),sQuery(id+"F16.wireOp",EDGE,"E86")])],"isStart":false}),makeQuery(id+"F17.opExtrude","CAP_FACE",FACE,{"disambiguationData":[OSD([sQuery(id+"F16.wireOp",EDGE,"E88.MirrorCS"),sQuery(id+"F16.wireOp",EDGE,"E89.MirrorCS"),sQuery(id+"F16.wireOp",EDGE,"E90.MirrorCS"),sQuery(id+"F16.wireOp",EDGE,"E91.MirrorCS"),sQuery(id+"F16.wireOp",EDGE,"E92.MirrorCS"),sQuery(id+"F16.wireOp",EDGE,"E95.MirrorCS"),sQuery(id+"F16.wireOp",EDGE,"E96.MirrorC")])],"isStart":false})]);}
            extrude(context, id + "F18", {"entities" : qUnion([Q0]), "endBound" : BoundingType.UP_TO_SURFACE, "endBoundEntityFace" : qUnion([Q1]), "depth" : 25 * mm});
        }
    });
